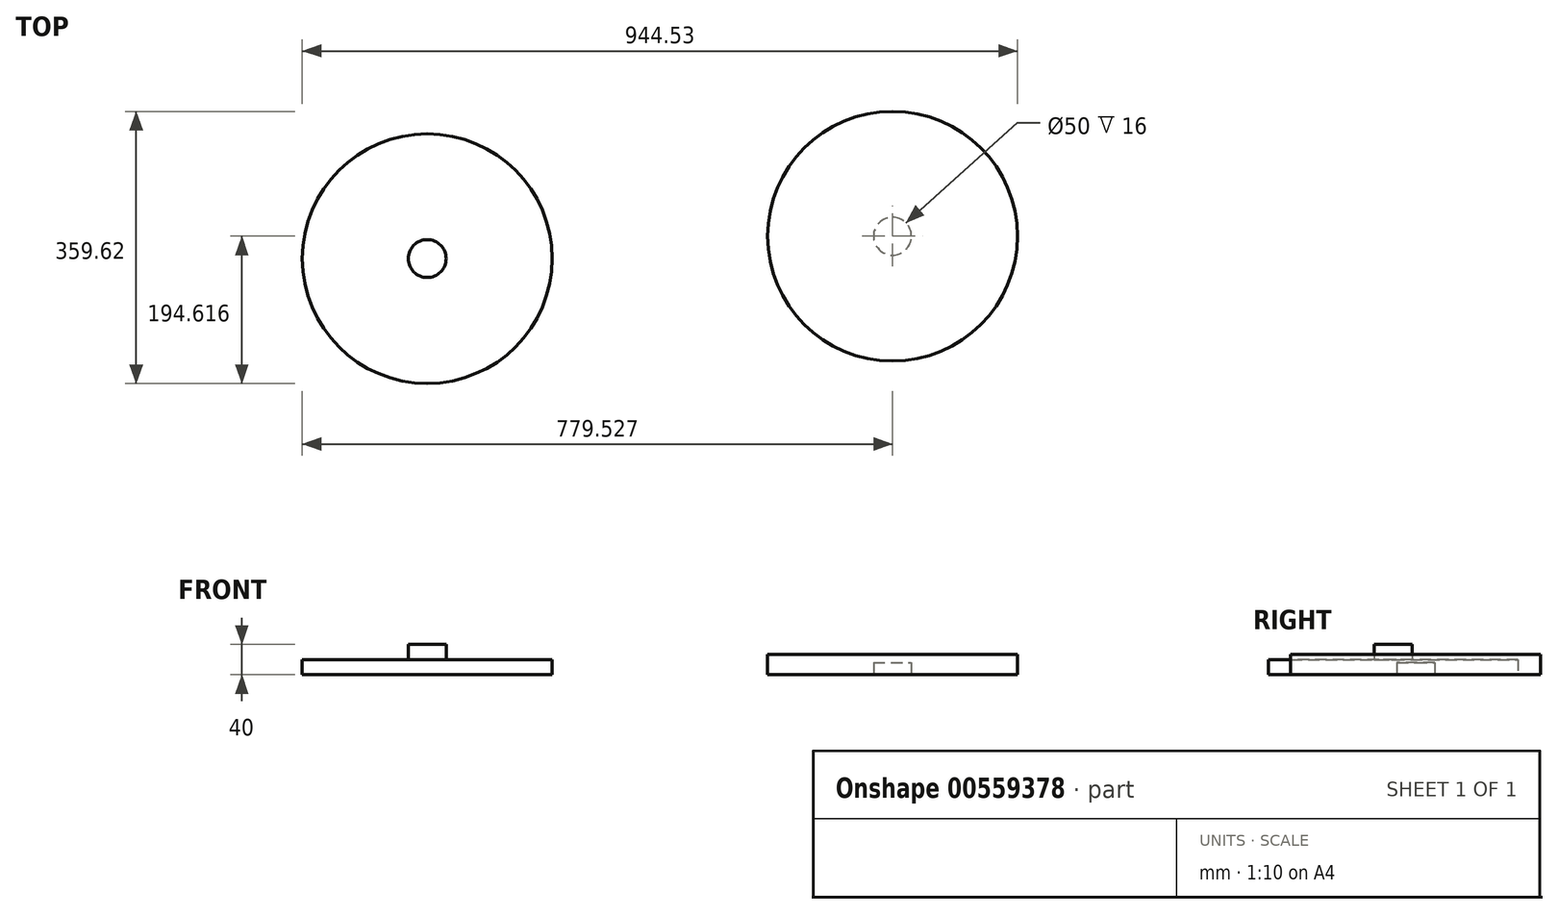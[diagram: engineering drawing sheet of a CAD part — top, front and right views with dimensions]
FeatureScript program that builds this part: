
annotation { "Feature Type Name" : "Feature", "Feature Type Description" : "" }
export const myFeature = defineFeature(function(context is Context, id is Id, definition is map)
    precondition{}
    {
        {
            var Q0;
            Q0=qCreatedBy(makeId("Top.planeOp"),FACE);
            var sketch = newSketch(context, id + "F0", { "sketchPlane" : qUnion([Q0])});
            skCircle(sketch, "E0", {"center": v(-352.57, 0) * mm, "radius": 165 * mm});
            skSolve(sketch);
        }
        {
            var Q0;
            Q0=makeQuery(id+"F0.imprint","IMPRINT",FACE,{"disambiguationData":[TD([[makeQuery(id+"F0.imprint","IMPRINT",EDGE,{"derivedFrom":sQuery(id+"F0.wireOp",EDGE,"E0")}),1.0]])]});
            extrude(context, id + "F1", {"entities" : qUnion([Q0]), "depth" : 20 * mm, "offsetDistance" : 25 * mm});
        }
        {
            var Q0;
            Q0=qCreatedBy(makeId("Top.planeOp"),FACE);
            var sketch = newSketch(context, id + "F2", { "sketchPlane" : qUnion([Q0])});
            skCircle(sketch, "E1", {"center": v(261.96, 29.62) * mm, "radius": 165 * mm});
            skSolve(sketch);
        }
        {
            var Q0;
            Q0=makeQuery(id+"F2.imprint","IMPRINT",FACE,{"disambiguationData":[TD([[makeQuery(id+"F2.imprint","IMPRINT",EDGE,{"derivedFrom":sQuery(id+"F2.wireOp",EDGE,"E1")}),1.0]])]});
            extrude(context, id + "F3", {"entities" : qUnion([Q0]), "depth" : 27 * mm, "offsetDistance" : 25 * mm});
        }
        {
            var Q0;
            Q0=makeQuery(id+"F1.opExtrude","CAP_FACE",FACE,{"disambiguationData":[OSD([sQuery(id+"F0.wireOp",EDGE,"E0")])],"isStart":false});
            var sketch = newSketch(context, id + "F4", { "sketchPlane" : qUnion([Q0])});
            skCircle(sketch, "E2", {"center": v(-352.57, 0) * mm, "radius": 25 * mm});
            skSolve(sketch);
        }
        {
            var Q0;
            Q0=makeQuery(id+"F4.imprint","IMPRINT",FACE,{"disambiguationData":[TD([[makeQuery(id+"F4.imprint","IMPRINT",EDGE,{"derivedFrom":sQuery(id+"F4.wireOp",EDGE,"E2")}),1.0]])]});
            extrude(context, id + "F5", {"entities" : qUnion([Q0]), "operationType" : NewBodyOperationType.ADD, "depth" : 20 * mm, "offsetDistance" : 25 * mm});
        }
        {
            var Q0;
            Q0=makeQuery(id+"F3.opExtrude","CAP_FACE",FACE,{"disambiguationData":[OSD([sQuery(id+"F2.wireOp",EDGE,"E1")])],"isStart":true});
            var sketch = newSketch(context, id + "F6", { "sketchPlane" : qUnion([Q0])});
            skCircle(sketch, "E3", {"center": v(261.96, -29.62) * mm, "radius": 25 * mm});
            skSolve(sketch);
        }
        {
            var Q0;
            Q0=makeQuery(id+"F6.imprint","IMPRINT",FACE,{"disambiguationData":[TD([[makeQuery(id+"F6.imprint","IMPRINT",EDGE,{"derivedFrom":sQuery(id+"F6.wireOp",EDGE,"E3")}),1.0]])]});
            extrude(context, id + "F7", {"entities" : qUnion([Q0]), "operationType" : NewBodyOperationType.REMOVE, "oppositeDirection" : true, "depth" : 16 * mm, "offsetDistance" : 25 * mm});
        }
    });
